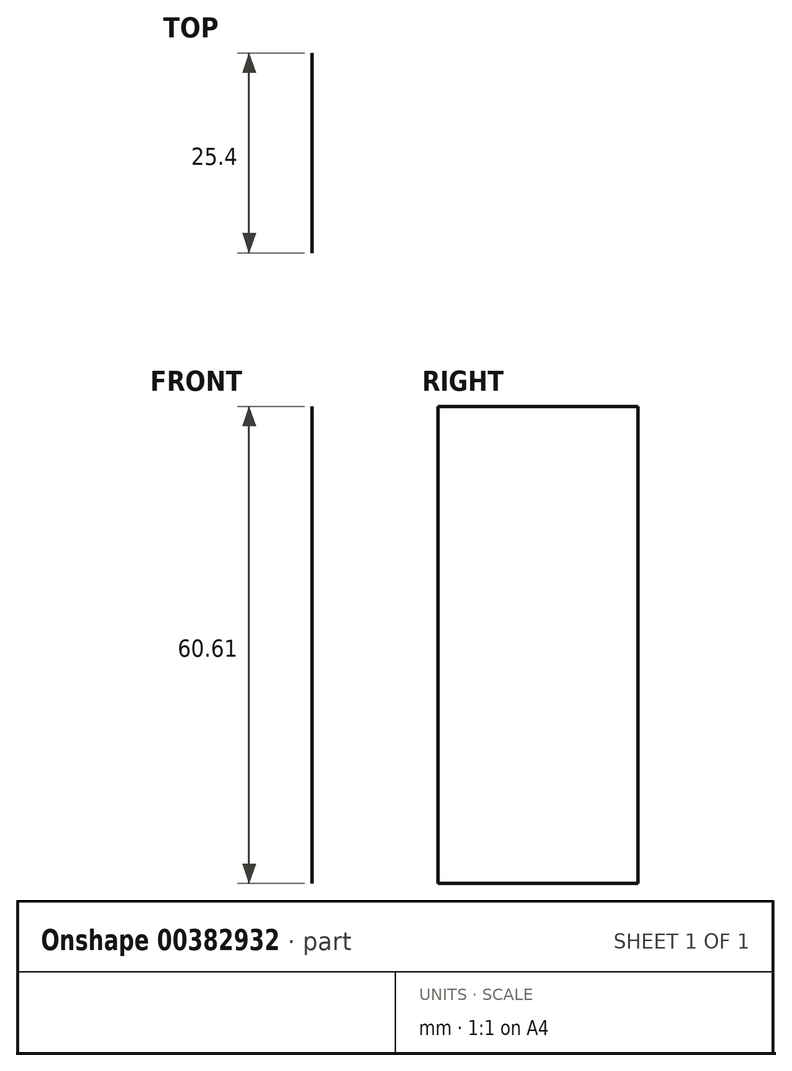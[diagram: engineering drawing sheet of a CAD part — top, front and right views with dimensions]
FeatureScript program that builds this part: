
annotation { "Feature Type Name" : "Feature", "Feature Type Description" : "" }
export const myFeature = defineFeature(function(context is Context, id is Id, definition is map)
    precondition{}
    {
        {
            var Q0;
            Q0=qCreatedBy(makeId("Front.planeOp"),FACE);
            var sketch = newSketch(context, id + "F0", { "sketchPlane" : qUnion([Q0])});
            skCircle(sketch, "E0", {"center": v(0, 0) * mm, "radius": 127 * mm});
            skLineSegment(sketch, "E1", {"start": v(0, 0) * mm, "end": v(0, 60.61) * mm});
            skSolve(sketch);
        }
        {
            var Q0;
            Q0=sQuery(id+"F0.wireOp",EDGE,"E1");
            extrude(context, id + "F1", {"bodyType" : ToolBodyType.SURFACE, "surfaceEntities" : qUnion([Q0]), "depth" : 25.4 * mm});
        }
    });
